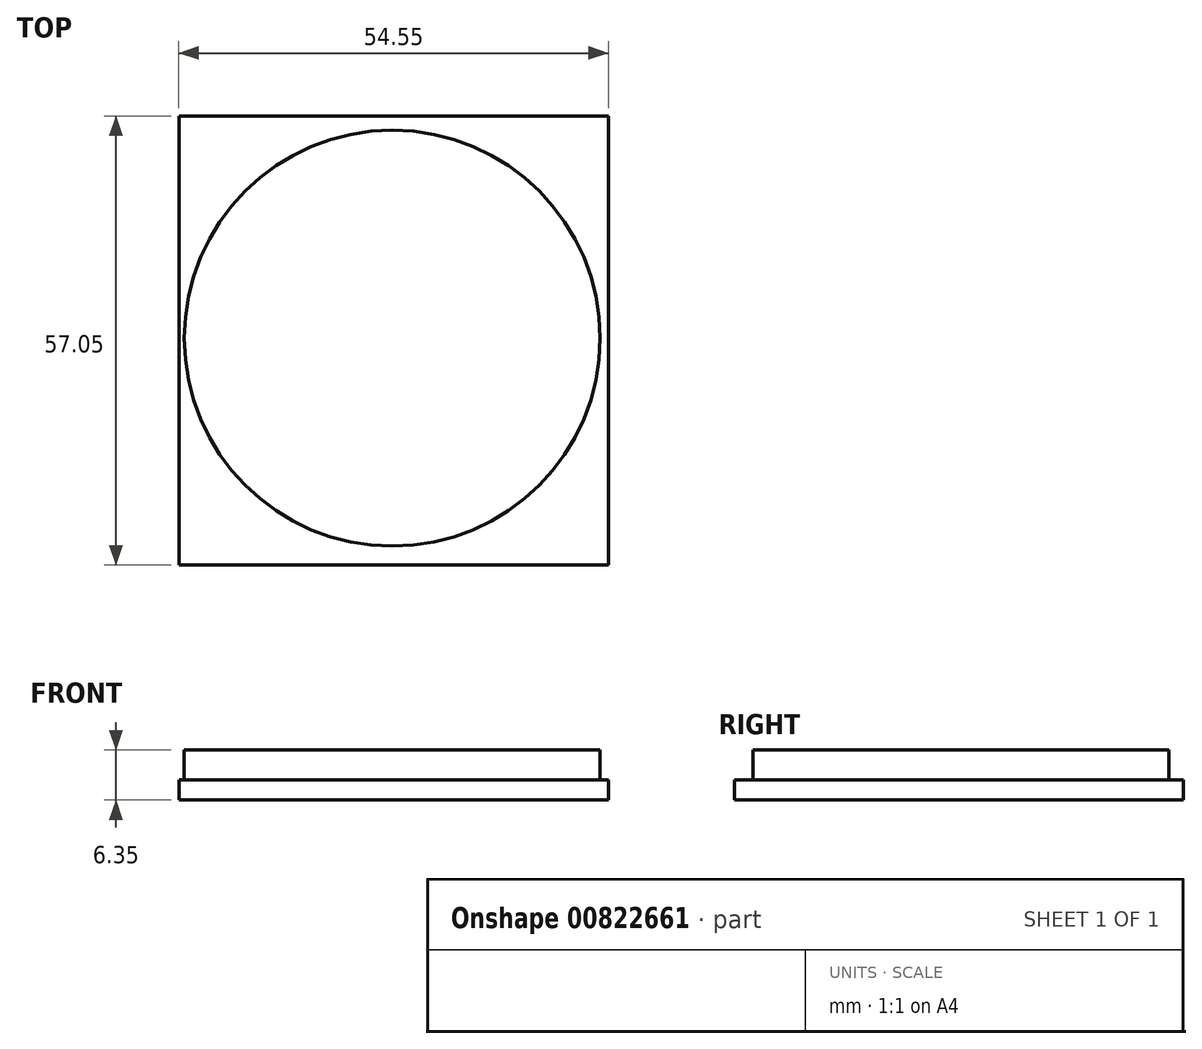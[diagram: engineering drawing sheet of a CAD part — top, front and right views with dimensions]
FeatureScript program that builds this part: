
annotation { "Feature Type Name" : "Feature", "Feature Type Description" : "" }
export const myFeature = defineFeature(function(context is Context, id is Id, definition is map)
    precondition{}
    {
        {
            var Q0;
            Q0=qCreatedBy(makeId("Front.planeOp"),FACE);
            var sketch = newSketch(context, id + "F0", { "sketchPlane" : qUnion([Q0])});
            skLineSegment(sketch, "E0", {"start": v(0, 74.7) * mm, "end": v(0, -90.4) * mm});
            skArc(sketch, "E1", {"start": v(-30.3, -84.44) * mm, "mid": v(-30.15, -88.44) * mm, "end": v(-26.67, -90.4) * mm});
            skArc(sketch, "E2", {"start": v(-30.3, -55.48) * mm, "mid": v(-31.94, -69.96) * mm, "end": v(-30.3, -84.44) * mm});
            skArc(sketch, "E3", {"start": v(-30.3, -26.04) * mm, "mid": v(-31.93, -40.76) * mm, "end": v(-30.3, -55.48) * mm});
            skArc(sketch, "E4", {"start": v(-30.3, 0) * mm, "mid": v(-32.02, -13.02) * mm, "end": v(-30.3, -26.04) * mm});
            skArc(sketch, "E5", {"start": v(-30.3, 25.64) * mm, "mid": v(-31.95, 12.82) * mm, "end": v(-30.3, 0) * mm});
            skArc(sketch, "E6", {"start": v(-30.3, 50.17) * mm, "mid": v(-31.98, 37.9) * mm, "end": v(-30.3, 25.64) * mm});
            skArc(sketch, "E7", {"start": v(-30.3, 74.56) * mm, "mid": v(-31.97, 62.37) * mm, "end": v(-30.3, 50.17) * mm});
            skLineSegment(sketch, "E8", {"start": v(-26.67, -90.4) * mm, "end": v(0, -90.4) * mm});
            skLineSegment(sketch, "E9", {"start": v(-30.3, 74.56) * mm, "end": v(0, 74.7) * mm});
            skSolve(sketch);
        }
        {
            var Q0;
            Q0 = qSketchRegion(id + "F0", true);
            var Q1;
            Q1=sQuery(id+"F0.wireOp",EDGE,"E0");
            revolve(context, id + "F1", {"surfaceOperationType" : NewSurfaceOperationType.NEW, "entities" : qUnion([Q0]), "axis" : qUnion([Q1]), "revolveType" : RevolveType.FULL});
        }
        {
            var Q0;
            Q0=makeQuery(id+"F1.opRevolve","SWEPT_FACE",FACE,{"disambiguationData":[OSD([sQuery(id+"F0.wireOp",EDGE,"E8")])]});
            extrude(context, id + "F2", {"entities" : qUnion([Q0]), "operationType" : NewBodyOperationType.REMOVE, "endBound" : BoundingType.THROUGH_ALL, "oppositeDirection" : true, "depth" : 25.4 * mm, "offsetDistance" : 25.4 * mm});
        }
        {
            var Q0;
            Q0=qCreatedBy(makeId("Front.planeOp"),FACE);
            var sketch = newSketch(context, id + "F3", { "sketchPlane" : qUnion([Q0])});
            skText(sketch, "E10", { "text": "C", "fontName": "DroidSansMono.ttf"});
            skText(sketch, "E11", { "text": "U", "fontName": "DroidSansMono.ttf"});
            skText(sketch, "E12", { "text": "P", "fontName": "DroidSansMono.ttf"});
            skText(sketch, "E13", { "text": "S", "fontName": "DroidSansMono.ttf"});
            const initialGuessF3  = {"E10": [-0.01554, 0.04073, 1, 0, 0.03108], "E11": [-0.01554, -0.00043, 1, 0, 0.03791], "E12": [-0.01554, -0.04206, 1, 0, 0.03818], "E13": [-0.01554, -0.08634, 1, 0, 0.03838]};
            skSetInitialGuess(sketch, initialGuessF3);
            skSolve(sketch);
        }
        {
            var Q0;
            Q0 = qSketchRegion(id + "F3", true);
            extrude(context, id + "F4", {"entities" : qUnion([Q0]), "operationType" : NewBodyOperationType.REMOVE, "endBound" : BoundingType.SYMMETRIC, "oppositeDirection" : true, "depth" : 254 * mm, "offsetDistance" : 25.4 * mm});
        }
        {
            var Q0;
            Q0=makeQuery(id+"F4.boolean.opBoolean","SPLIT",BODY,{"disambiguationData":[OD(2.0)],"derivedFrom":makeQuery(id+"F1.opRevolve","SWEPT_BODY",BODY,{"disambiguationData":[OSD([sQuery(id+"F0.wireOp",EDGE,"E0"),sQuery(id+"F0.wireOp",EDGE,"E1"),sQuery(id+"F0.wireOp",EDGE,"E2"),sQuery(id+"F0.wireOp",EDGE,"E3"),sQuery(id+"F0.wireOp",EDGE,"E4"),sQuery(id+"F0.wireOp",EDGE,"E5"),sQuery(id+"F0.wireOp",EDGE,"E6"),sQuery(id+"F0.wireOp",EDGE,"E7"),sQuery(id+"F0.wireOp",EDGE,"E8"),sQuery(id+"F0.wireOp",EDGE,"E9")])]})});
            var Q1;
            Q1=makeQuery(id+"F4.boolean.opBoolean","SPLIT",BODY,{"disambiguationData":[OD(1.0)],"derivedFrom":makeQuery(id+"F1.opRevolve","SWEPT_BODY",BODY,{"disambiguationData":[OSD([sQuery(id+"F0.wireOp",EDGE,"E0"),sQuery(id+"F0.wireOp",EDGE,"E1"),sQuery(id+"F0.wireOp",EDGE,"E2"),sQuery(id+"F0.wireOp",EDGE,"E3"),sQuery(id+"F0.wireOp",EDGE,"E4"),sQuery(id+"F0.wireOp",EDGE,"E5"),sQuery(id+"F0.wireOp",EDGE,"E6"),sQuery(id+"F0.wireOp",EDGE,"E7"),sQuery(id+"F0.wireOp",EDGE,"E8"),sQuery(id+"F0.wireOp",EDGE,"E9")])]})});
            deleteBodies(context, id + "F5", {"entities" : qUnion([Q0, Q1])});
        }
        {
            var Q0;
            Q0=qCreatedBy(makeId("Top.planeOp"),FACE);
            var sketch = newSketch(context, id + "F6", { "sketchPlane" : qUnion([Q0])});
            skCircle(sketch, "E14", {"center": v(-111.36, -5.46) * mm, "radius": 26.42 * mm});
            skSolve(sketch);
        }
        {
            var Q0;
            Q0 = qSketchRegion(id + "F6", true);
            extrude(context, id + "F7", {"entities" : qUnion([Q0]), "depth" : 3.8 * mm, "offsetDistance" : 25.4 * mm});
        }
        {
            var Q0;
            Q0=qCreatedBy(makeId("Top.planeOp"),FACE);
            var sketch = newSketch(context, id + "F8", { "sketchPlane" : qUnion([Q0])});
            skLineSegment(sketch, "E15.bottom", {"start": v(-138.47, -34.27) * mm, "end": v(-83.92, -34.27) * mm});
            skLineSegment(sketch, "E15.top", {"start": v(-138.47, 22.78) * mm, "end": v(-83.92, 22.78) * mm});
            skLineSegment(sketch, "E15.left", {"start": v(-138.47, -34.27) * mm, "end": v(-138.47, 22.78) * mm});
            skLineSegment(sketch, "E15.right", {"start": v(-83.92, -34.27) * mm, "end": v(-83.92, 22.78) * mm});
            skLineSegment(sketch, "E16", {"start": v(-138.47, 16.42) * mm, "end": v(-131.8, 22.78) * mm});
            skLineSegment(sketch, "E17", {"start": v(-92.58, 22.78) * mm, "end": v(-83.92, 15.8) * mm});
            skLineSegment(sketch, "E18", {"start": v(-138.47, -26.97) * mm, "end": v(-131.48, -34.27) * mm});
            skLineSegment(sketch, "E19", {"start": v(-90.8, -34.27) * mm, "end": v(-83.92, -27.39) * mm});
            skSolve(sketch);
        }
        {
            var Q0;
            Q0 = qSketchRegion(id + "F8", true);
            var Q1;
            Q1=makeQuery(id+"F7.opExtrude","CAP_FACE",FACE,{"disambiguationData":[OSD([sQuery(id+"F6.wireOp",EDGE,"E14")])],"isStart":true});
            extrude(context, id + "F9", {"entities" : qUnion([Q0]), "operationType" : NewBodyOperationType.ADD, "oppositeDirection" : true, "depth" : 2.54 * mm, "endBoundEntityFace" : qUnion([Q1]), "offsetDistance" : 25.4 * mm});
        }
    });
